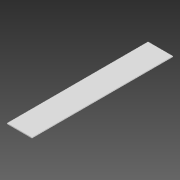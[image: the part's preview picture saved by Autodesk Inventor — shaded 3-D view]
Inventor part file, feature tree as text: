
AUTODESK INVENTOR PART (.ipt)
format: ipt  version: 2020 (Build 240168000, 168)  size: 74,240 bytes
history: native  units: in
note: dims shown in document units (in); Inventor stores cm internally (conversion verified against a paired STEP export)
features: extrude x1, sketch x1
ambient origin geometry x8: Origin, YZ Plane, XZ Plane, XY Plane, X Axis, Y Axis, Z Axis, Center Point
bodies: Solid1 (feature_tree)
feature tree (2):
  extrude  "Extrusion1"  Depth=24.6063in
  sketch  "Sketch1"  dims[d0=4.3307in d1=24.6063in d2=0.1181in d3=0.0in]
